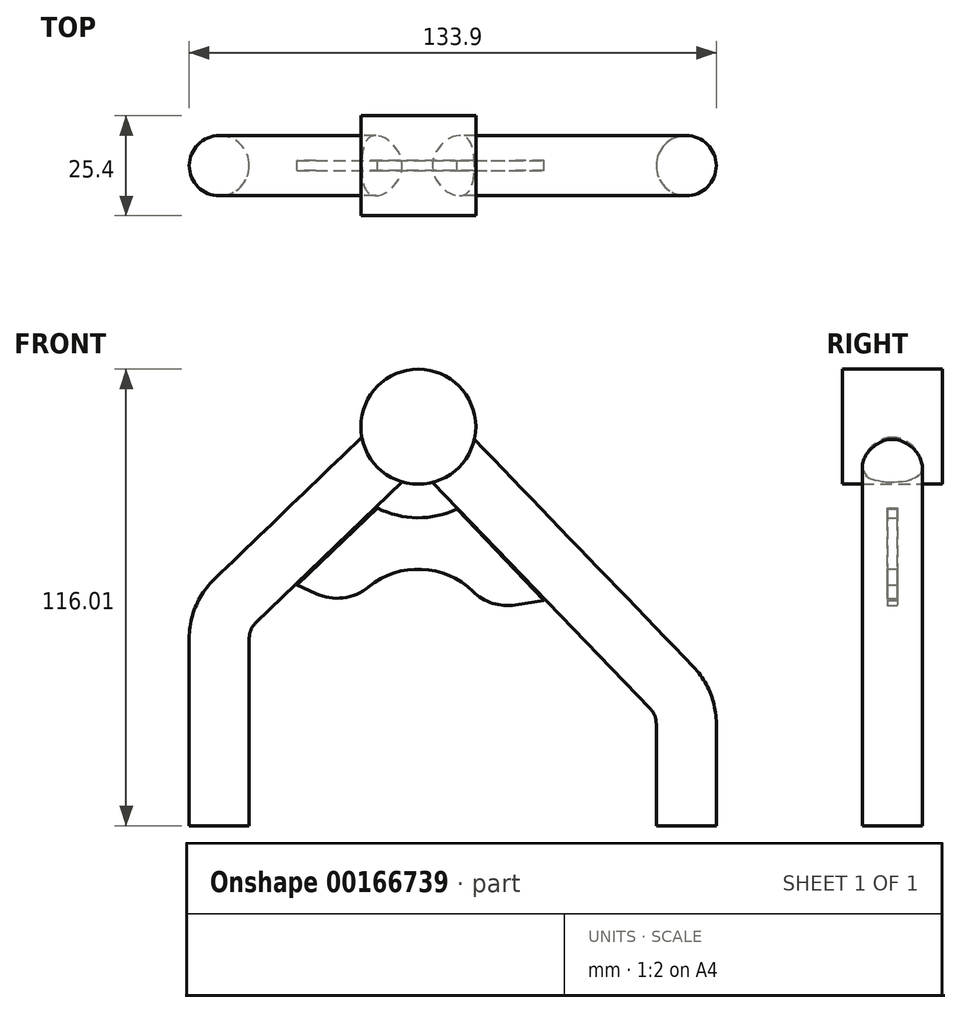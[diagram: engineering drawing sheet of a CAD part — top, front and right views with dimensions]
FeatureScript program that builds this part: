
annotation { "Feature Type Name" : "Feature", "Feature Type Description" : "" }
export const myFeature = defineFeature(function(context is Context, id is Id, definition is map)
    precondition{}
    {
        {
            var Q0;
            Q0=qCreatedBy(makeId("Front.planeOp"),FACE);
            var sketch = newSketch(context, id + "F0", { "sketchPlane" : qUnion([Q0])});
            skLineSegment(sketch, "E0", {"start": v(0, 0) * mm, "end": v(-46.27, -44.56) * mm});
            skLineSegment(sketch, "E1", {"start": v(-50.16, -53.71) * mm, "end": v(-50.16, -101.4) * mm});
            skLineSegment(sketch, "E2", {"start": v(0, 0) * mm, "end": v(64.13, -66.6) * mm});
            skLineSegment(sketch, "E3", {"start": v(67.69, -75.4) * mm, "end": v(67.69, -101.4) * mm});
            skPoint(sketch, "E4.visualSharp", {"position": v(-50.16, -48.3) * mm});
            skArc(sketch, "E4.filletArc", {"start": v(-46.27, -44.56) * mm, "mid": v(-49.15, -48.74) * mm, "end": v(-50.16, -53.71) * mm});
            skPoint(sketch, "E5.visualSharp", {"position": v(67.69, -70.28) * mm});
            skArc(sketch, "E5.filletArc", {"start": v(67.69, -75.4) * mm, "mid": v(66.77, -70.65) * mm, "end": v(64.13, -66.6) * mm});
            skSolve(sketch);
        }
        {
            var Q0;
            Q0=sQuery(id+"F0.wireOp",EDGE,"E3");
            var Q1;
            Q1=sQuery(id+"F0.wireOp",VERTEX,"E3.end");
            cPlane(context, id + "F1", {"entities" : qUnion([Q0, Q1]), "cplaneType" : CPlaneType.CURVE_POINT, "offset" : 25.4 * mm, "width" : 152.4 * mm, "height" : 152.4 * mm});
        }
        {
            var Q0;
            Q0=qCreatedBy(id+"F1.planeOp",FACE);
            var sketch = newSketch(context, id + "F2", { "sketchPlane" : qUnion([Q0])});
            skCircle(sketch, "E6", {"center": v(68.08, 0) * mm, "radius": 7.63 * mm});
            skSolve(sketch);
        }
        {
            var Q0;
            Q0=qCreatedBy(makeId("Front.planeOp"),FACE);
            var sketch = newSketch(context, id + "F3", { "sketchPlane" : qUnion([Q0])});
            skCircle(sketch, "E7", {"center": v(0, 0) * mm, "radius": 14.6 * mm});
            skSolve(sketch);
        }
        {
            var Q0;
            Q0=makeQuery(id+"F3.imprint","IMPRINT",FACE,{"disambiguationData":[TD([[makeQuery(id+"F3.imprint","IMPRINT",EDGE,{"derivedFrom":sQuery(id+"F3.wireOp",EDGE,"E7")}),1.0]])]});
            extrude(context, id + "F4", {"entities" : qUnion([Q0]), "endBound" : BoundingType.SYMMETRIC, "depth" : 25.4 * mm});
        }
        {
            var Q0;
            Q0=makeQuery(id+"F2.imprint","IMPRINT",FACE,{"disambiguationData":[TD([[makeQuery(id+"F2.imprint","IMPRINT",EDGE,{"derivedFrom":sQuery(id+"F2.wireOp",EDGE,"E6")}),1.0]])]});
            var Q1;
            Q1=sQuery(id+"F0.wireOp",EDGE,"E3");
            var Q2;
            Q2=sQuery(id+"F0.wireOp",EDGE,"E5.filletArc");
            var Q3;
            Q3=sQuery(id+"F0.wireOp",EDGE,"E2");
            var Q4;
            Q4=sQuery(id+"F0.wireOp",EDGE,"E0");
            var Q5;
            Q5=sQuery(id+"F0.wireOp",EDGE,"E4.filletArc");
            var Q6;
            Q6=sQuery(id+"F0.wireOp",EDGE,"E1");
            sweep(context, id + "F5", {"operationType" : NewBodyOperationType.ADD, "profiles" : qUnion([Q0]), "path" : qUnion([Q1, Q2, Q3, Q4, Q5, Q6])});
        }
        {
            var Q0;
            Q0=qCreatedBy(makeId("Front.planeOp"),FACE);
            var sketch = newSketch(context, id + "F6", { "sketchPlane" : qUnion([Q0])});
            skArc(sketch, "E8", {"start": v(-10.4, -20.67) * mm, "mid": v(-0.28, -23.13) * mm, "end": v(9.89, -20.91) * mm});
            skArc(sketch, "E9", {"start": v(13.88, -41.85) * mm, "mid": v(0.86, -36.22) * mm, "end": v(-12.6, -40.7) * mm});
            skLineSegment(sketch, "E10", {"start": v(9.89, -20.91) * mm, "end": v(31.97, -44.18) * mm});
            skLineSegment(sketch, "E11", {"start": v(31.97, -44.18) * mm, "end": v(24.7, -45.31) * mm});
            skLineSegment(sketch, "E12", {"start": v(-26.06, -42.37) * mm, "end": v(-30.74, -40.17) * mm});
            skLineSegment(sketch, "E13", {"start": v(-30.74, -40.17) * mm, "end": v(-10.4, -20.67) * mm});
            skPoint(sketch, "E14.visualSharp", {"position": v(17.39, -46.45) * mm});
            skArc(sketch, "E14.filletArc", {"start": v(13.88, -41.85) * mm, "mid": v(18.89, -44.86) * mm, "end": v(24.7, -45.31) * mm});
            skPoint(sketch, "E15.visualSharp", {"position": v(-17.39, -46.45) * mm});
            skArc(sketch, "E15.filletArc", {"start": v(-26.06, -42.37) * mm, "mid": v(-19.09, -43.49) * mm, "end": v(-12.6, -40.7) * mm});
            skSolve(sketch);
        }
        {
            var Q0;
            Q0=makeQuery(id+"F6.imprint","IMPRINT",FACE,{"disambiguationData":[TD([[makeQuery(id+"F6.imprint","IMPRINT",EDGE,{"derivedFrom":sQuery(id+"F6.wireOp",EDGE,"E8")}),-1.0]])]});
            extrude(context, id + "F7", {"entities" : qUnion([Q0]), "operationType" : NewBodyOperationType.ADD, "endBound" : BoundingType.SYMMETRIC, "depth" : 2.54 * mm});
        }
    });
